# Revit family: BROWNLEE - 2680 INNIE - 20 IN PENDANT
name_source: partatom
category: Lighting Fixtures
revit_build: Autodesk Revit 2017 (Build: 20160225_1515(x64)
units: mm (PartAtom-declared; Revit-internal decimal feet)

## family parameters
Always vertical = Yes
Cut with Voids When Loaded = No
Host = Ceiling
Light Source = Yes
OmniClass Number = 23.80.70.11
OmniClass Title = Luminaries for Internal Lighting
Part Type = Normal
Room Calculation Point = No
Round Connector Dimension = Use Diameter
Shared = No

## types (1)
- 20 IN PENDANT
    Color Filter = 16777215
    Description = Suspended LED with inset diffuser, customizable finishes
    Dimming Lamp Color Temperature Shift = <None>
    Inner Finish = BROWNLEE LIGHTING - FINISH - BLACK
    Lens = BROWLEE LIGHTING - ACRYLIC LENS
    Manufacturer = Brownlee Lighting
    Model = 2680-20-C34-35K
    Outer Finish = BROWNLEE LIGHTING - FINISH - BLACK
    Photometric Web File = 2680-20-C34-35K.ies
    Power Drop = BROWNLEE LIGHTING - CORD - BLACK
    Tilt Angle = 90.00°
    URL = www.brownlee.com

## geometry (parser evidence)
native form markers: Sweep x11
no freeform markers — native parametric forms only
